# Revit family: BIMLIB_Термоголовка_TW_РОСТерм
name_source: partatom
category: Арматура трубопроводов
revit_build: Autodesk Revit 2017 (Build: 20170118_1100(x64)
units: mm (PartAtom-declared; Revit-internal decimal feet)

## family parameters
Всегда вертикально = Нет
На основе рабочей плоскости = Да
Общий = Нет
При загрузке вырезать с полостями = Нет
Размер круглого соединителя = Использовать диаметр
Тип детали = Датчик

## types (1)
- HEIZEN TW
    ADSK_URL документации изделия = http://rostherm.ru
    ADSK_URL страницы изделия = http://rostherm.ru
    ADSK_Версия Revit = 2017
    ADSK_Единица измерения = шт.
    ADSK_Завод-изготовитель = Heizen
    ADSK_Масса = 0
    ADSK_Материал = BIMLIB_Белый_пластик_РТ
    ADSK_Наименование краткое = Heizen TW-1
    BL_BIM library = https://bimlib.pro
    URL = http://rostherm.ru
    Изготовитель = РОСТерм
    Коэффициент K = 0
    Описание = Термостатическая головка Heizen (Хейзен) серии TW-1 устанавливается на термостатический клапан с помощью резьбового соединения, подкрученного в ручную на корпус клапана.
    Отметка по умолчанию = 1219.2 мм
    РТ_D/2 = 15 мм
    РТ_Материал_Основание = BIMLIB_Серый_пластик_РТ
